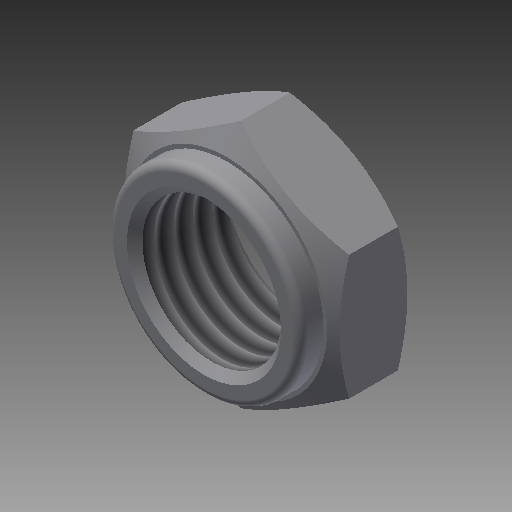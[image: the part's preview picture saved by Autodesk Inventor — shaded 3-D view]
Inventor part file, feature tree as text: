
AUTODESK INVENTOR PART (.ipt)
format: ipt  version: 2019 (Build 230136000, 136)  size: 190,976 bytes
history: native  units: mm
features: extrude x2, sketch x2, other x2, hole x1, thread x1, chamfer x1, revolve x1, fillet x1
ambient origin geometry x8: Origin, YZ Plane, XZ Plane, XY Plane, X Axis, Y Axis, Z Axis, Center Point
bodies: Solido1 (feature_tree)
feature tree (11):
  extrude  "Estrusione1"  Depth=14.0mm
  extrude  "Estrusione2"  Depth=5.0mm TaperAngle=0.0deg
  sketch  "Schizzo3"
  other  "Piano di lavoro1"
  hole  "Foro1"  [1 undecoded]
  thread  "Filettatura1"
  chamfer  "Smusso1"  Distance=12.5mm
  revolve  "Rivoluzione2"
  fillet  "Raccordo1"  [1 undecoded]
  sketch  "Schizzo1"
  other  "Linea chiusa proiettata1"
note: 2 required parameter values undecoded (feature->parameter linkage not recoverable at this tier; creation-order binding heuristic only, values carry confidence <= 0.55)
